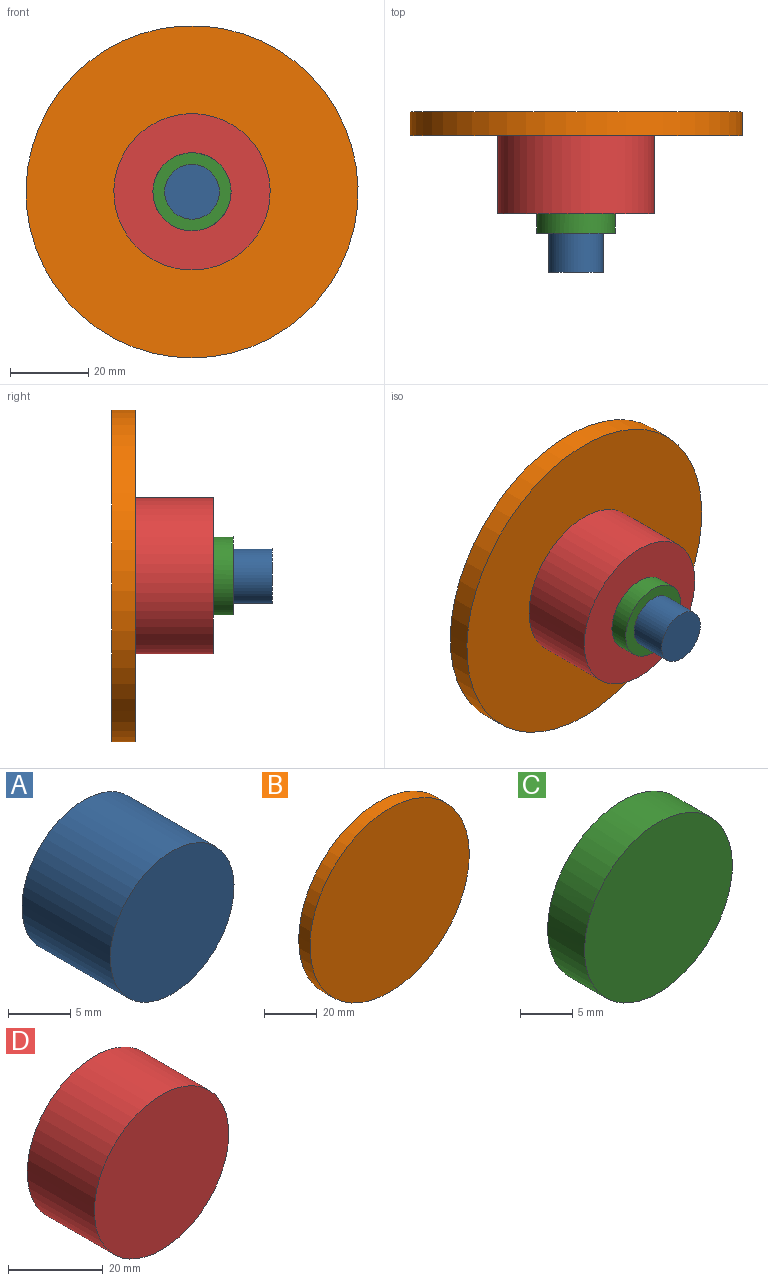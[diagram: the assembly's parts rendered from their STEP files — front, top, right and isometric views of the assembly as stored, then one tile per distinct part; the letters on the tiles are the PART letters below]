
ASSEMBLY  parts=4 mates=3
PART A: 3 faces, bbox 14x10x14 mm
  f0: cylinder r=7mm len=14mm, axis (0,1,0), area 439.8mm2, adj f1,f2
  f1: plane 14x14mm, normal (0,-1,0), area 153.9mm2, adj f0
  f2: plane 14x14mm, normal (0,1,0), area 153.9mm2, adj f0
PART B: 3 faces, bbox 85x6x85 mm
  f0: cylinder r=42.5mm len=85mm, axis (0,1,0), area 1602.2mm2, adj f1,f2
  f1: plane 85x85mm, normal (0,-1,0), area 5674.5mm2, adj f0
  f2: plane 85x85mm, normal (0,1,0), area 5674.5mm2, adj f0
PART C: 3 faces, bbox 20x5x20 mm
  f0: cylinder r=10mm len=20mm, axis (0,-1,0), area 314.2mm2, adj f1,f2
  f1: plane 20x20mm, normal (0,-1,0), area 314.2mm2, adj f0
  f2: plane 20x20mm, normal (0,1,0), area 314.2mm2, adj f0
PART D: 3 faces, bbox 40x20x40 mm
  f0: cylinder r=20mm len=40mm, axis (0,1,0), area 2513.3mm2, adj f1,f2
  f1: plane 40x40mm, normal (0,-1,0), area 1256.6mm2, adj f0
  f2: plane 40x40mm, normal (0,1,0), area 1256.6mm2, adj f0
PLACE A t=(-29.3,-45.56,21.92)mm
PLACE B t=(-29.3,-14.56,21.92)mm
PLACE C t=(-29.3,-40.56,21.92)mm
PLACE D t=(-29.3,-20.56,21.92)mm
MATE fastened B.f0 <-> D.f0  axis (0,-1,0) through (-29.3,-20.56,21.92)mm
MATE fastened C.f0 <-> D.f0  axis (0,1,0) through (-29.3,-40.56,21.92)mm
MATE fastened A.f0 <-> C.f0  axis (0,1,0) through (-29.3,-45.56,21.92)mm
